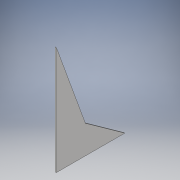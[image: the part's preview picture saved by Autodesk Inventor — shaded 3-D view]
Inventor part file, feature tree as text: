
AUTODESK INVENTOR PART (.ipt)
format: ipt  version: 2017 (Build 210142000, 142)  size: 91,648 bytes
history: native  units: in
note: dims shown in document units (in); Inventor stores cm internally (conversion verified against a paired STEP export)
features: extrude x1, sketch x1
ambient origin geometry x8: Origin, YZ Plane, XZ Plane, XY Plane, X Axis, Y Axis, Z Axis, Center Point
bodies: Solid1 (feature_tree)
feature tree (2):
  extrude  "Extrusion1"  Depth=3.0in
  sketch  "Sketch1"  dims[d0=4.75in d1=3.0in d2=0.05in d3=0.0in]
